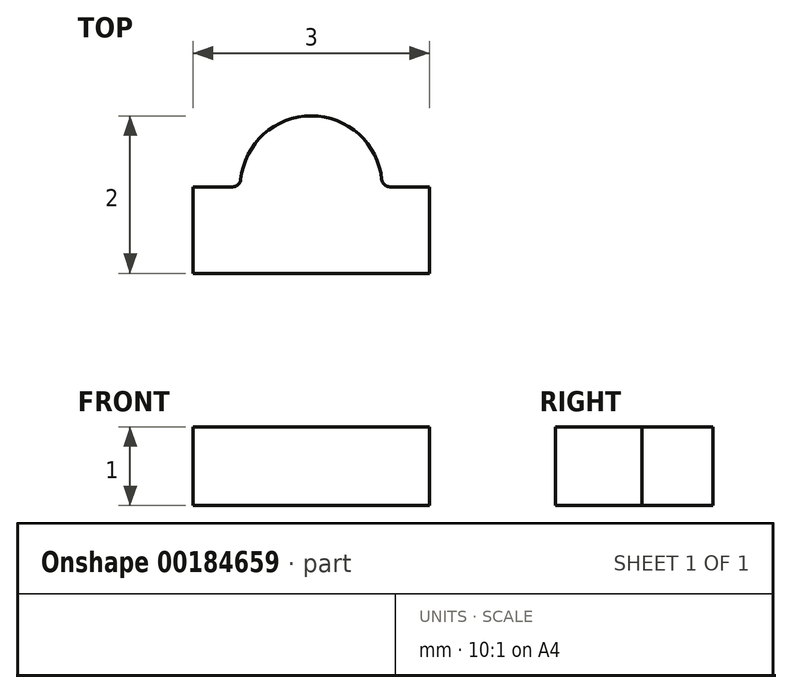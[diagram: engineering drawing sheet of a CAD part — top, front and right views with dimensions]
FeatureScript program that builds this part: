
annotation { "Feature Type Name" : "Feature", "Feature Type Description" : "" }
export const myFeature = defineFeature(function(context is Context, id is Id, definition is map)
    precondition{}
    {
        {
            var Q0;
            Q0=qCreatedBy(makeId("Top.planeOp"),FACE);
            var sketch = newSketch(context, id + "F0", { "sketchPlane" : qUnion([Q0])});
            skLineSegment(sketch, "E0", {"start": v(0, 0) * mm, "end": v(-1.5, 0) * mm});
            skLineSegment(sketch, "E1", {"start": v(-1.5, 0) * mm, "end": v(-1.5, 1.1) * mm});
            skLineSegment(sketch, "E2", {"start": v(-1.5, 1.1) * mm, "end": v(-1, 1.1) * mm});
            skLineSegment(sketch, "E3", {"start": v(0, 1.1) * mm, "end": v(0, 0) * mm});
            skArc(sketch, "E4", {"start": v(0, 2) * mm, "mid": v(-0.6, 1.77) * mm, "end": v(-0.9, 1.2) * mm});
            skLineSegment(sketch, "E5", {"start": v(0, 2) * mm, "end": v(0, 1.1) * mm});
            skPoint(sketch, "E6.visualSharp", {"position": v(-0.9, 1.1) * mm});
            skArc(sketch, "E6.filletArc", {"start": v(-1, 1.1) * mm, "mid": v(-0.93, 1.13) * mm, "end": v(-0.9, 1.2) * mm});
            skSolve(sketch);
        }
        {
            var Q0;
            Q0 = qSketchRegion(id + "F0", true);
            extrude(context, id + "F1", {"entities" : qUnion([Q0]), "depth" : 1 * mm, "offsetDistance" : 25 * mm});
        }
        {
            var Q0;
            Q0=makeQuery(id+"F1.opExtrude","SWEPT_BODY",BODY,{"disambiguationData":[OSD([sQuery(id+"F0.wireOp",EDGE,"E0"),sQuery(id+"F0.wireOp",EDGE,"E1"),sQuery(id+"F0.wireOp",EDGE,"E2"),sQuery(id+"F0.wireOp",EDGE,"E3"),sQuery(id+"F0.wireOp",EDGE,"E4"),sQuery(id+"F0.wireOp",EDGE,"E5"),sQuery(id+"F0.wireOp",EDGE,"E6.filletArc")])]});
            var Q1;
            Q1=qCreatedBy(makeId("Right.planeOp"),FACE);
            mirror(context, id + "F2", {"operationType" : NewBodyOperationType.ADD, "entities" : qUnion([Q0]), "mirrorPlane" : qUnion([Q1])});
        }
    });
